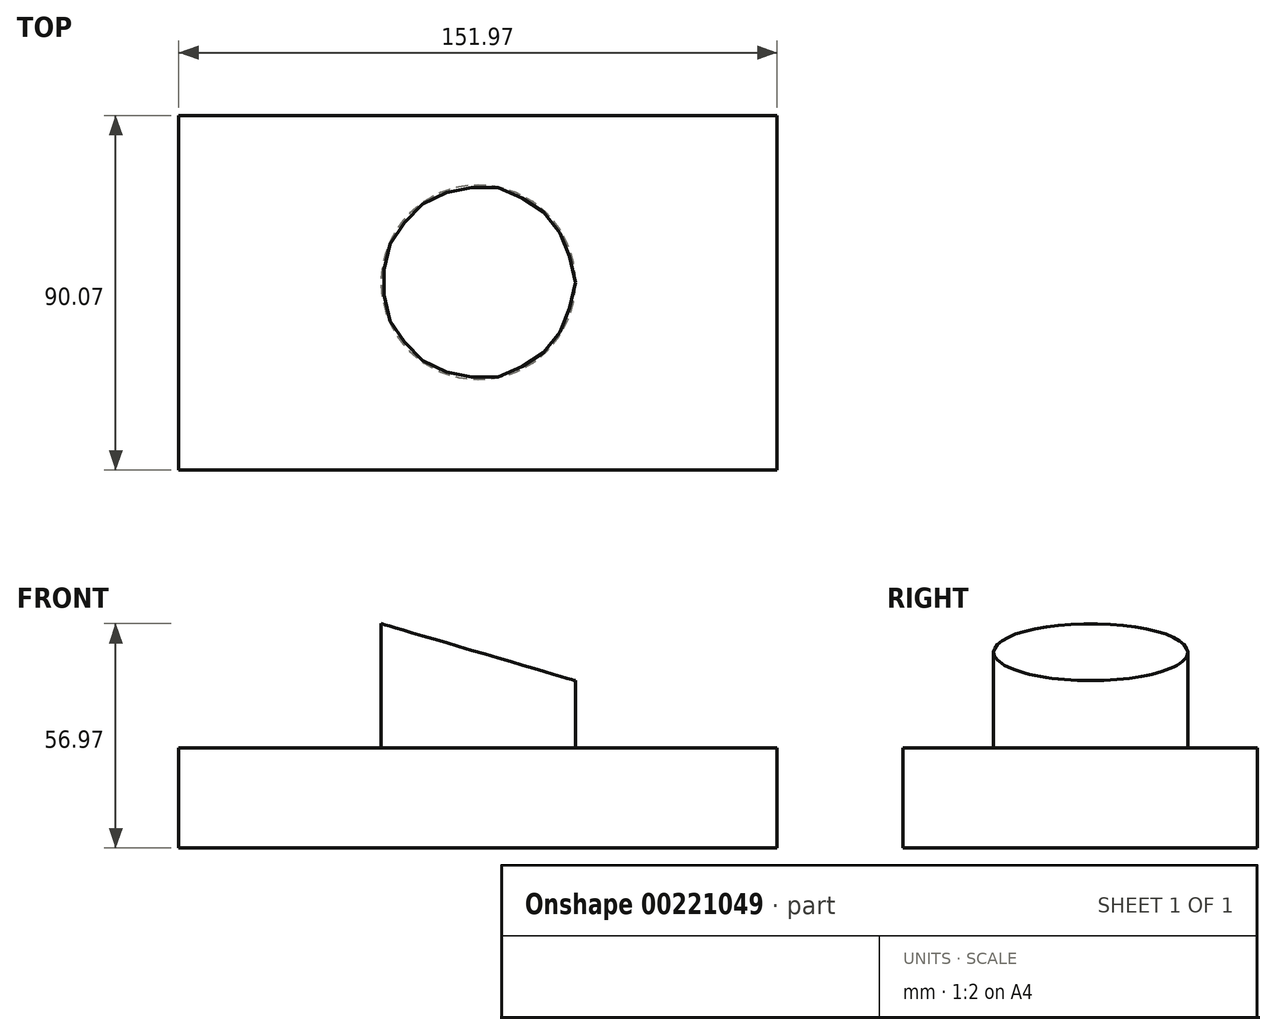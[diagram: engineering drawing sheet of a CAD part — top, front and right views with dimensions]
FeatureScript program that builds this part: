
annotation { "Feature Type Name" : "Feature", "Feature Type Description" : "" }
export const myFeature = defineFeature(function(context is Context, id is Id, definition is map)
    precondition{}
    {
        {
            var Q0;
            Q0=qCreatedBy(makeId("Top.planeOp"),FACE);
            var sketch = newSketch(context, id + "F0", { "sketchPlane" : qUnion([Q0])});
            skLineSegment(sketch, "E0.bottom", {"start": v(-76.08, 41.87) * mm, "end": v(75.89, 41.87) * mm});
            skLineSegment(sketch, "E0.top", {"start": v(-76.08, -48.2) * mm, "end": v(75.89, -48.2) * mm});
            skLineSegment(sketch, "E0.left", {"start": v(-76.08, 41.87) * mm, "end": v(-76.08, -48.2) * mm});
            skLineSegment(sketch, "E0.right", {"start": v(75.89, 41.87) * mm, "end": v(75.89, -48.2) * mm});
            skSolve(sketch);
        }
        {
            var Q0;
            Q0=makeQuery(id+"F0.imprint","IMPRINT",FACE,{"disambiguationData":[TD([[makeQuery(id+"F0.imprint","IMPRINT",EDGE,{"derivedFrom":sQuery(id+"F0.wireOp",EDGE,"E0.bottom")}),-1.0]])]});
            extrude(context, id + "F1", {"entities" : qUnion([Q0]), "depth" : 25.4 * mm});
        }
        {
            var Q0;
            Q0=makeQuery(id+"F1.opExtrude","CAP_FACE",FACE,{"disambiguationData":[OSD([sQuery(id+"F0.wireOp",EDGE,"E0.bottom"),sQuery(id+"F0.wireOp",EDGE,"E0.top"),sQuery(id+"F0.wireOp",EDGE,"E0.left"),sQuery(id+"F0.wireOp",EDGE,"E0.right")])],"isStart":false});
            var sketch = newSketch(context, id + "F2", { "sketchPlane" : qUnion([Q0])});
            skCircle(sketch, "E1", {"center": v(0, -0.48) * mm, "radius": 24.68 * mm});
            skSolve(sketch);
        }
        {
            var Q0;
            Q0=makeQuery(id+"F2.imprint","IMPRINT",FACE,{"disambiguationData":[TD([[makeQuery(id+"F2.imprint","IMPRINT",EDGE,{"derivedFrom":sQuery(id+"F2.wireOp",EDGE,"E1")}),1.0]])]});
            extrude(context, id + "F3", {"entities" : qUnion([Q0]), "operationType" : NewBodyOperationType.ADD, "depth" : 38.1 * mm});
        }
        {
            var Q0;
            Q0=makeQuery(id+"F1.opExtrude","SWEPT_FACE",FACE,{"disambiguationData":[OSD([sQuery(id+"F0.wireOp",EDGE,"E0.top")])]});
            var sketch = newSketch(context, id + "F4", { "sketchPlane" : qUnion([Q0])});
            skLineSegment(sketch, "E2", {"start": v(-56.15, 66.21) * mm, "end": v(38.52, 38.42) * mm});
            skLineSegment(sketch, "E3", {"start": v(38.52, 38.42) * mm, "end": v(29.13, 74.64) * mm});
            skLineSegment(sketch, "E4", {"start": v(29.13, 74.64) * mm, "end": v(-56.15, 66.21) * mm});
            skSolve(sketch);
        }
        {
            var Q0;
            Q0 = qSketchRegion(id + "F4", true);
            extrude(context, id + "F5", {"entities" : qUnion([Q0]), "operationType" : NewBodyOperationType.REMOVE, "endBound" : BoundingType.THROUGH_ALL, "oppositeDirection" : true, "depth" : 25.4 * mm});
        }
    });
